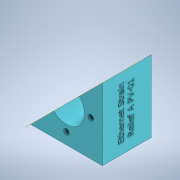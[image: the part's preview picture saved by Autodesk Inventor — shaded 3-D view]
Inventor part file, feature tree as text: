
AUTODESK INVENTOR PART (.ipt)
format: ipt  version: 2022.1 (Build 261234000, 234)  size: 931,840 bytes
history: native  units: mm
features: sketch x7, extrude x2, revolve x2, emboss x2, hole x1, plane x1, split x1
ambient origin geometry x8: Origin, YZ Plane, XZ Plane, XY Plane, X Axis, Y Axis, Z Axis, Center Point
bodies: Solid7 (feature_tree)
feature tree (16):
  extrude  "Extrusion20"  Depth=50.0mm
  revolve  "Revolution4"  [1 undecoded]
  extrude  "Extrusion21"  TaperAngle=90.0deg  [1 undecoded]
  revolve  "Revolution5"  [1 undecoded]
  hole  "Hole2"  [1 undecoded]
  plane  "Work Plane6"
  emboss  "Emboss3"
  emboss  "Emboss4"
  split  "Split1"
  sketch  "Sketch27"  dims[d124=50.0mm d125=50.0mm]
  sketch  "Sketch28"  dims[d126=29.0mm d127=0.0mm d128=3.0mm]
  sketch  "Sketch29"  dims[d129=12.5mm d130=90.0deg]
  sketch  "Sketch30"  dims[d131=5.0mm d132=0.0mm d133=2.5mm]
  sketch  "Sketch31"  dims[d134=90.0deg d135=34.0mm]
  sketch  "Sketch32"  dims[d136=34.0mm]
  sketch  "Sketch33"  dims[d137=3.797mm d138=6.0mm d139=11.43mm d140=15.24mm d141=14.3117mm d142=8.0mm d143=20.594885mm d144=1.0mm d145=0.0mm d146=1.0mm d147=0.0mm]
note: 4 required parameter values undecoded (feature->parameter linkage not recoverable at this tier; creation-order binding heuristic only, values carry confidence <= 0.55)